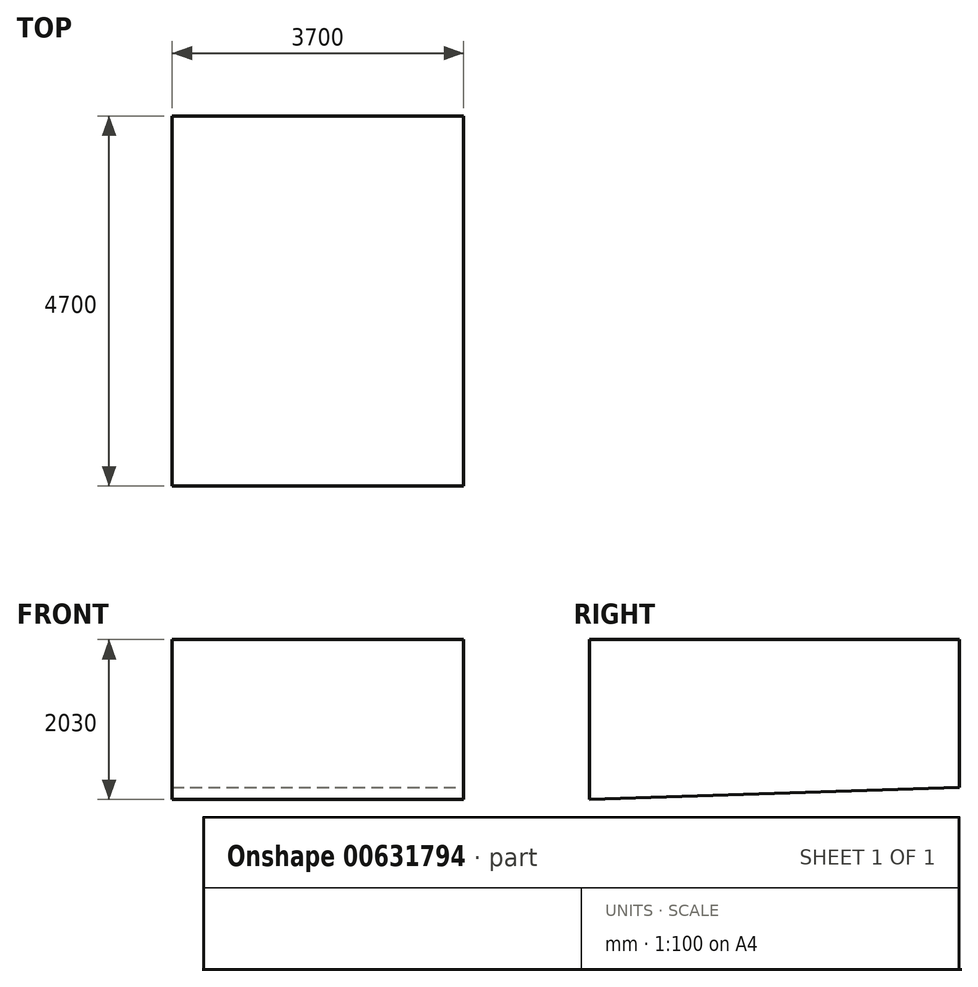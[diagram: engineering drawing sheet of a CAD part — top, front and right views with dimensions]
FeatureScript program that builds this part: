
annotation { "Feature Type Name" : "Feature", "Feature Type Description" : "" }
export const myFeature = defineFeature(function(context is Context, id is Id, definition is map)
    precondition{}
    {
        {
            var Q0;
            Q0=qCreatedBy(makeId("Top.planeOp"),FACE);
            var sketch = newSketch(context, id + "F0", { "sketchPlane" : qUnion([Q0])});
            skLineSegment(sketch, "E0.bottom", {"start": v(0, 0) * mm, "end": v(3700, 0) * mm});
            skLineSegment(sketch, "E0.top", {"start": v(0, 4700) * mm, "end": v(3700, 4700) * mm});
            skLineSegment(sketch, "E0.left", {"start": v(0, 0) * mm, "end": v(0, 4700) * mm});
            skLineSegment(sketch, "E0.right", {"start": v(3700, 0) * mm, "end": v(3700, 4700) * mm});
            skSolve(sketch);
        }
        {
            var Q0;
            Q0=makeQuery(id+"F0.imprint","IMPRINT",FACE,{"disambiguationData":[TD([[makeQuery(id+"F0.imprint","IMPRINT",EDGE,{"derivedFrom":sQuery(id+"F0.wireOp",EDGE,"E0.bottom")}),1.0]])]});
            extrude(context, id + "F1", {"entities" : qUnion([Q0]), "depth" : 1520 * mm, "offsetDistance" : 25 * mm});
        }
        {
            var Q0;
            Q0=makeQuery(id+"F1.opExtrude","SWEPT_FACE",FACE,{"disambiguationData":[OSD([sQuery(id+"F0.wireOp",EDGE,"E0.right")])]});
            var sketch = newSketch(context, id + "F2", { "sketchPlane" : qUnion([Q0])});
            skLineSegment(sketch, "E1", {"start": v(0, 0) * mm, "end": v(0, -510) * mm});
            skLineSegment(sketch, "E2", {"start": v(4700, -360) * mm, "end": v(4700, 0) * mm});
            skLineSegment(sketch, "E3", {"start": v(4700, -360) * mm, "end": v(0, -510) * mm});
            skSolve(sketch);
        }
        {
            var Q0;
            Q0=makeQuery(id+"F2.imprint","IMPRINT",FACE,{"disambiguationData":[TD([[makeQuery(id+"F2.imprint","IMPRINT",EDGE,{"derivedFrom":sQuery(id+"F2.wireOp",EDGE,"E1")}),1.0]])]});
            var Q1;
            Q1=makeQuery(id+"F1.opExtrude","SWEPT_FACE",FACE,{"disambiguationData":[OSD([sQuery(id+"F0.wireOp",EDGE,"E0.left")])]});
            extrude(context, id + "F3", {"entities" : qUnion([Q0]), "operationType" : NewBodyOperationType.ADD, "oppositeDirection" : true, "depth" : 3700 * mm, "endBoundEntityFace" : qUnion([Q1]), "offsetDistance" : 25 * mm});
        }
        {
            var Q0;
            Q0=makeQuery(id+"F1.opExtrude","SWEPT_FACE",FACE,{"disambiguationData":[OSD([sQuery(id+"F0.wireOp",EDGE,"E0.bottom")])]});
            var sketch = newSketch(context, id + "F4", { "sketchPlane" : qUnion([Q0])});
            skLineSegment(sketch, "E4", {"start": v(1850, 2290) * mm, "end": v(-88.77, 1483.05) * mm});
            skLineSegment(sketch, "E5", {"start": v(-88.77, 1483.05) * mm, "end": v(1850, 2290) * mm});
            skLineSegment(sketch, "E6", {"start": v(3788.77, 1483.05) * mm, "end": v(1850, 2290) * mm});
            skLineSegment(sketch, "E7", {"start": v(1850, -510) * mm, "end": v(1850, 2290) * mm});
            skLineSegment(sketch, "E8", {"start": v(0, 1520) * mm, "end": v(0, 3701.03) * mm, "construction": true});
            skSolve(sketch);
        }
        {
            var Q0;
            Q0=sQuery(id+"F4.wireOp",EDGE,"E4");
            var Q1;
            Q1=sQuery(id+"F4.wireOp",EDGE,"E6");
            extrude(context, id + "F5", {"bodyType" : ToolBodyType.SURFACE, "surfaceEntities" : qUnion([Q0, Q1]), "oppositeDirection" : true, "depth" : 4793.45 * mm, "offsetDistance" : 25 * mm});
        }
    });
